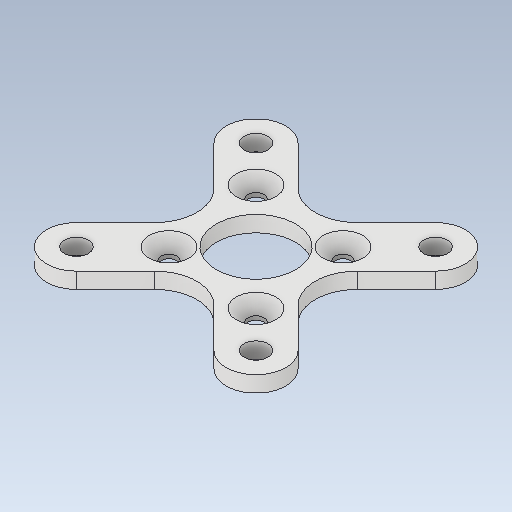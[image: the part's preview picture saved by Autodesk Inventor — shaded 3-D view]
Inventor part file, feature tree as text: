
AUTODESK INVENTOR PART (.ipt)
format: ipt  version: 2020.2 (Build 242310000, 310)  size: 149,504 bytes
history: imported  units: mm
features: imported_body x1
ambient origin geometry x8: Origin, YZ Plane, XZ Plane, XY Plane, X Axis, Y Axis, Z Axis, Center Point
bodies: Solide1 (imported_parasolid), Body1 (imported_parasolid)
feature tree (1):
  imported_body  NMx_Import_Brep_tag  [imported B-rep: ~31 faces, bbox_mm=[27.930718, 2.0, 27.930718]]
